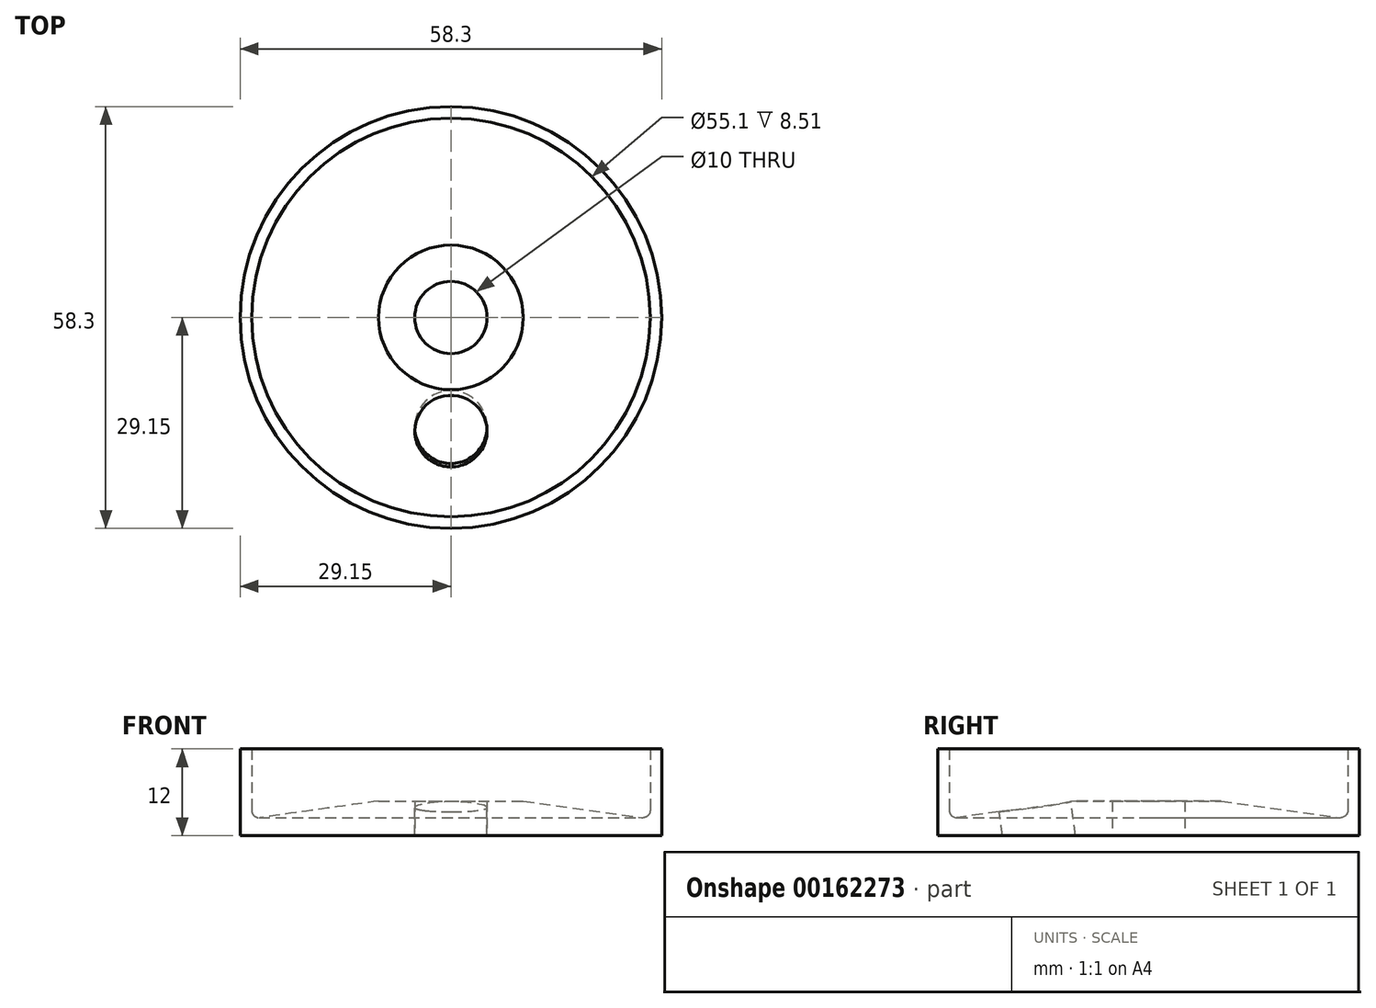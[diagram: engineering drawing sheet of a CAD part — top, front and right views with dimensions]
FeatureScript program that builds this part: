
annotation { "Feature Type Name" : "Feature", "Feature Type Description" : "" }
export const myFeature = defineFeature(function(context is Context, id is Id, definition is map)
    precondition{}
    {
        {
            var Q0;
            Q0=qCreatedBy(makeId("Right.planeOp"),FACE);
            var sketch = newSketch(context, id + "F0", { "sketchPlane" : qUnion([Q0])});
            skLineSegment(sketch, "E0", {"start": v(0, 0) * mm, "end": v(0, 22.16) * mm, "construction": true});
            skLineSegment(sketch, "E1", {"start": v(0, 4.8) * mm, "end": v(-10, 4.8) * mm});
            skLineSegment(sketch, "E2", {"start": v(-29.15, 0) * mm, "end": v(-29.15, 12) * mm});
            skLineSegment(sketch, "E3", {"start": v(-29.15, 12) * mm, "end": v(-27.55, 12) * mm});
            skLineSegment(sketch, "E4", {"start": v(-27.55, 12) * mm, "end": v(-27.55, 3.5) * mm});
            skLineSegment(sketch, "E5", {"start": v(-29.15, 0) * mm, "end": v(0, 0) * mm});
            skLineSegment(sketch, "E6", {"start": v(0, 4.8) * mm, "end": v(0, 0) * mm});
            skPoint(sketch, "E7.visualSharp", {"position": v(-27.55, 2.69) * mm});
            skArc(sketch, "E7.filletArc", {"start": v(-27.55, 3.5) * mm, "mid": v(-27.2, 2.74) * mm, "end": v(-26.41, 2.5) * mm});
            skLineSegment(sketch, "E8", {"start": v(-26.41, 2.5) * mm, "end": v(-10, 4.8) * mm});
            skLineSegment(sketch, "E9", {"start": v(-18.2, 3.65) * mm, "end": v(-15.91, -12.64) * mm, "construction": true});
            skSolve(sketch);
        }
        {
            var Q0;
            Q0 = qSketchRegion(id + "F0", true);
            var Q1;
            Q1=sQuery(id+"F0.wireOp",EDGE,"E0");
            revolve(context, id + "F1", {"entities" : qUnion([Q0]), "axis" : qUnion([Q1]), "revolveType" : RevolveType.FULL});
        }
        {
            var Q0;
            Q0=makeQuery(id+"F1.opRevolve","SWEPT_FACE",FACE,{"disambiguationData":[OSD([sQuery(id+"F0.wireOp",EDGE,"E5")])]});
            var sketch = newSketch(context, id + "F2", { "sketchPlane" : qUnion([Q0])});
            skCircle(sketch, "E10", {"center": v(0, 0) * mm, "radius": 5 * mm});
            skSolve(sketch);
        }
        {
            var Q0;
            Q0 = qSketchRegion(id + "F2", true);
            extrude(context, id + "F3", {"entities" : qUnion([Q0]), "operationType" : NewBodyOperationType.REMOVE, "endBound" : BoundingType.UP_TO_NEXT, "oppositeDirection" : true, "depth" : 25 * mm});
        }
        {
            var Q0;
            Q0=sQuery(id+"F0.wireOp",EDGE,"E8");
            cPlane(context, id + "F4", {"entities" : qUnion([Q0]), "cplaneType" : CPlaneType.LINE_ANGLE, "offset" : 25 * mm, "angle" : 0 * degree, "width" : 150 * mm, "height" : 150 * mm});
        }
        {
            var Q0;
            Q0=qCreatedBy(id+"F4.planeOp",FACE);
            var sketch = newSketch(context, id + "F5", { "sketchPlane" : qUnion([Q0])});
            skCircle(sketch, "E11", {"center": v(0, -15) * mm, "radius": 5 * mm});
            skLineSegment(sketch, "E12", {"start": v(0, 0) * mm, "end": v(0, -15) * mm, "construction": true});
            skSolve(sketch);
        }
        {
            var Q0;
            Q0 = qSketchRegion(id + "F5", true);
            extrude(context, id + "F6", {"entities" : qUnion([Q0]), "operationType" : NewBodyOperationType.REMOVE, "endBound" : BoundingType.UP_TO_NEXT, "oppositeDirection" : true, "depth" : 25 * mm});
        }
    });
